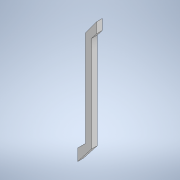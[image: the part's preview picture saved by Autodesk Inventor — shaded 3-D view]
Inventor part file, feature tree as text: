
AUTODESK INVENTOR PART (.ipt)
format: ipt  version: 2021 (Build 250183000, 183)  size: 107,520 bytes
history: native  units: mm
features: extrude x1, sketch x1
ambient origin geometry x8: Origin, YZ Plane, XZ Plane, XY Plane, X Axis, Y Axis, Z Axis, Center Point
bodies: Solide1 (feature_tree)
feature tree (2):
  extrude  "Extrusion1"  Depth=147.0mm
  sketch  "Esquisse1"
